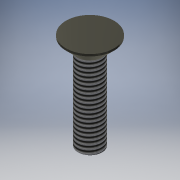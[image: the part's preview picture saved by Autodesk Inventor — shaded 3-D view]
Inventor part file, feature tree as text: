
AUTODESK INVENTOR PART (.ipt)
format: ipt  version: 2020.2 (Build 242310000, 310)  size: 135,680 bytes
history: native  units: mm
features: extrude x5, sketch x5, other x1, thread x1, chamfer x1
ambient origin geometry x1: Origin
bodies: Body1 (feature_tree)
feature tree (13):
  other  "ソリッド1"
  extrude  "押し出し1"  Depth=3.0mm
  extrude  "押し出し2"  Depth=6.0mm TaperAngle=0.0deg
  thread  "ねじ1"
  chamfer  "面取り1"  Distance=6.0mm
  extrude  "押し出し4"  Depth=1.75mm TaperAngle=0.0deg
  extrude  "押し出し5"  Depth=10.0mm TaperAngle=0.0deg
  extrude  "押し出し6"  Depth=1.5mm TaperAngle=45.0deg
  sketch  "スケッチ1"
  sketch  "スケッチ2"
  sketch  "スケッチ4"
  sketch  "スケッチ5"
  sketch  "スケッチ6"
